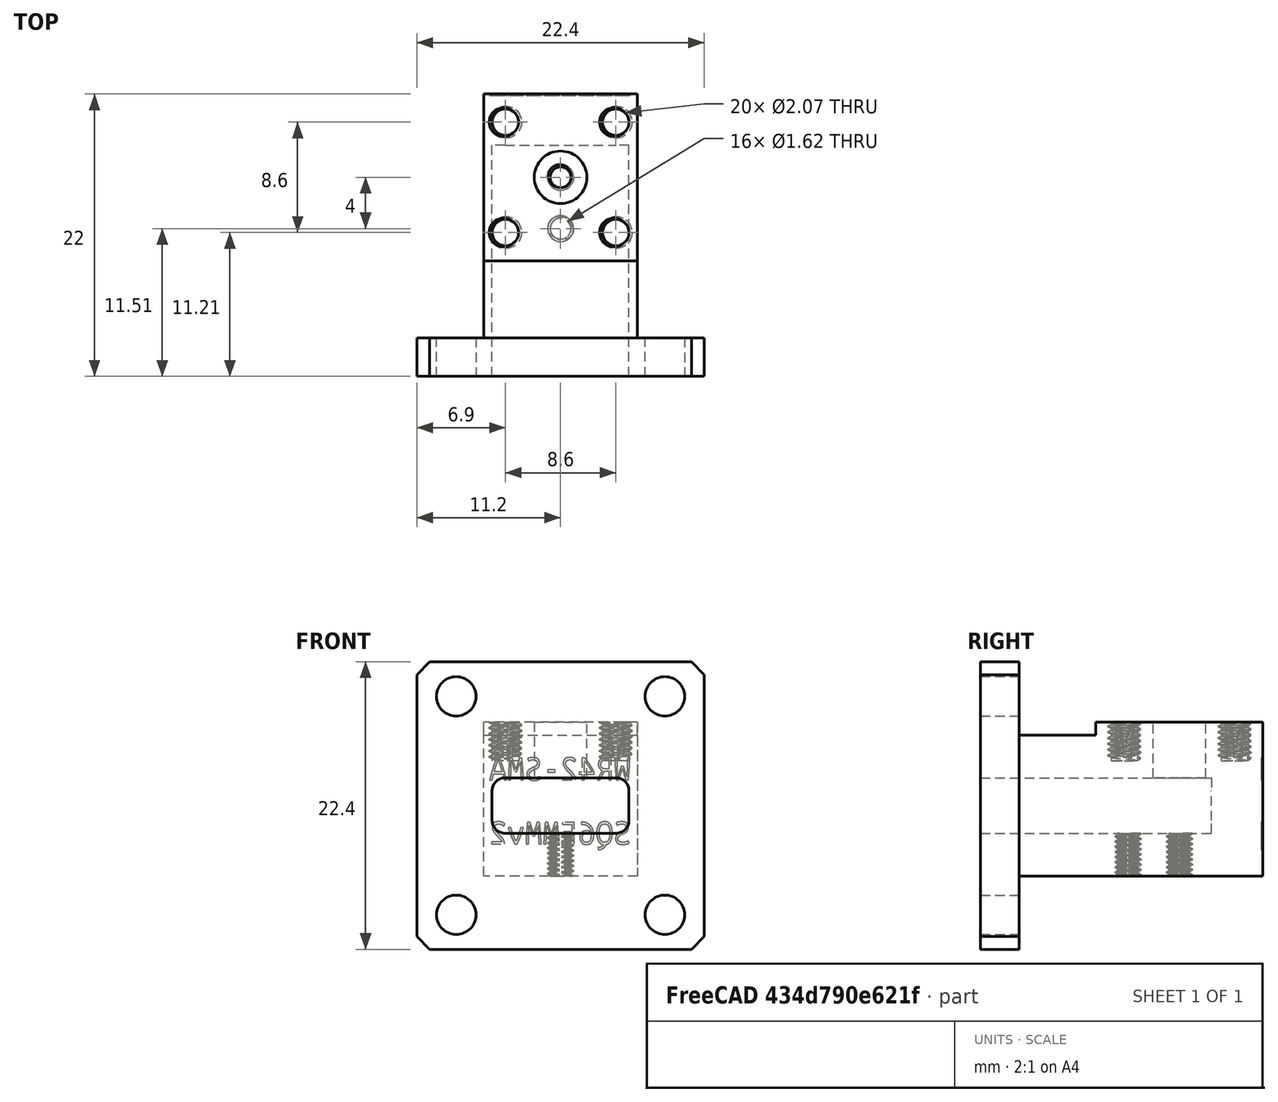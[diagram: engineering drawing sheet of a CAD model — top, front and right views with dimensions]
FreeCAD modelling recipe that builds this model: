
FCSTD DOCUMENT  (FreeCAD 1.0R38641 +468 (Git))
Label: WR42-SMA-narrow
License: All rights reserved
LicenseURL: https://en.wikipedia.org/wiki/All_rights_reserved
objects: Sketcher::SketchObject×7, PartDesign::Chamfer×4, PartDesign::Pocket×4, PartDesign::Pad×3, TechDraw::DrawViewPart×3, TechDraw::DrawViewBalloon×3, PartDesign::Hole×2, Part::Part2DObjectPython×2, TechDraw::DrawSVGTemplate×1, PartDesign::Body×1, TechDraw::DrawPage×1
note: 56 computed .brp shape members not serialized (recipe doc carries the construction recipe); baked Part::Feature solids carry a one-line shape summary decoded from their .brp

FEATURE [Sketcher::SketchObject] Sketch
  ArcFitTolerance = 0
  AttachmentSupport = -> [XZ_Plane]
  FullyConstrained = true
  MakeInternals = false
  MapMode = 5
  Placement = pos=(0,0,0) rot=(1,0,0;1.5708rad)
  sketch-geometry (9):
    g0: LineSegment StartX=-11.2 StartY=11.2 StartZ=0 EndX=-11.2 EndY=-11.2 EndZ=0
    g1: LineSegment StartX=-11.2 StartY=-11.2 StartZ=0 EndX=11.2 EndY=-11.2 EndZ=0
    g2: LineSegment StartX=11.2 StartY=-11.2 StartZ=0 EndX=11.2 EndY=11.2 EndZ=0
    g3: LineSegment StartX=11.2 StartY=11.2 StartZ=0 EndX=-11.2 EndY=11.2 EndZ=0
    g4: GeomPoint [constr] X=0 Y=0 Z=0
    g5: Circle CenterX=-8.13 CenterY=8.51 CenterZ=0 NormalX=0 NormalY=0 NormalZ=1 AngleXU=0 Radius=1.535
    g6: Circle CenterX=8.13 CenterY=8.51 CenterZ=0 NormalX=0 NormalY=0 NormalZ=1 AngleXU=0 Radius=1.535
    g7: Circle CenterX=8.13 CenterY=-8.51 CenterZ=0 NormalX=0 NormalY=0 NormalZ=1 AngleXU=0 Radius=1.535
    g8: Circle CenterX=-8.13 CenterY=-8.51 CenterZ=0 NormalX=0 NormalY=0 NormalZ=1 AngleXU=0 Radius=1.535
  constraints (24):
    c: Coincident(g0,g1)
    c: Coincident(g1,g2)
    c: Coincident(g2,g3)
    c: Coincident(g3,g0)
    c: Horizontal(g1)
    c: Horizontal(g3)
    c: Vertical(g0)
    c: Vertical(g2)
    c: Symmetric(g1,g0,g4)
    c: Coincident(g4,g-1)
    c: DistanceY(g2,g2) = 22.4
    c: DistanceX(g3,g3) = 22.4
    c: Diameter(g5) = 3.07
    c: Equal(g5,g6)
    c: Equal(g5,g8)
    c: Equal(g5,g7)
    c: DistanceX(g4,g6) = 8.13
    c: DistanceX(g5,g4) = 8.13
    c: DistanceX(g8,g4) = 8.13
    c: DistanceX(g4,g7) = 8.13
    c: DistanceY(g4,g5) = 8.51
    c: DistanceY(g4,g6) = 8.51
    c: DistanceY(g7,g4) = 8.51
    c: DistanceY(g8,g4) = 8.51
FEATURE [PartDesign::Pad] Pad
  Direction = (0,-1,2e-16)
  Length = 3
  Length2 = 10
  Placement = pos=(0,0,0) rot=(1,0,0;1.5708rad)
  Profile = -> Sketch
  ReferenceAxis = -> Sketch [N_Axis]
  Suppressed = false
  Type = 0
FEATURE [PartDesign::Chamfer] Chamfer
  Angle = 45
  Base = -> Pad [Edge8]
  BaseFeature = -> Pad
  ChamferType = 0
  FlipDirection = false
  Placement = pos=(0,0,0) rot=(1,0,0;1.5708rad)
  Size = 1
  Size2 = 1
  SupportTransform = false
  Suppressed = false
  UseAllEdges = false
FEATURE [PartDesign::Chamfer] Chamfer001
  Angle = 45
  Base = -> Chamfer [Edge23]
  BaseFeature = -> Chamfer
  ChamferType = 0
  FlipDirection = false
  Placement = pos=(0,0,0) rot=(1,0,0;1.5708rad)
  Size = 1
  Size2 = 1
  SupportTransform = false
  Suppressed = false
  UseAllEdges = false
FEATURE [PartDesign::Chamfer] Chamfer002
  Angle = 45
  Base = -> Chamfer001 [Edge20]
  BaseFeature = -> Chamfer001
  ChamferType = 0
  FlipDirection = false
  Placement = pos=(0,0,0) rot=(1,0,0;1.5708rad)
  Size = 1
  Size2 = 1
  SupportTransform = false
  Suppressed = false
  UseAllEdges = false
FEATURE [PartDesign::Chamfer] Chamfer003
  Angle = 45
  Base = -> Chamfer002 [Edge19]
  BaseFeature = -> Chamfer002
  ChamferType = 0
  FlipDirection = false
  Placement = pos=(0,0,0) rot=(1,0,0;1.5708rad)
  Size = 1
  Size2 = 1
  SupportTransform = false
  Suppressed = false
  UseAllEdges = false
FEATURE [Sketcher::SketchObject] Sketch001
  ArcFitTolerance = 0
  AttachmentSupport = -> [Chamfer003]
  ExternalGeometry = -> [Chamfer003]
  FullyConstrained = true
  MakeInternals = false
  MapMode = 5
  Placement = pos=(0,0,0) rot=(-1,0,0;1.5708rad)
  sketch-geometry (5):
    g0: LineSegment StartX=-6 StartY=5.5 StartZ=0 EndX=-6 EndY=-5.5 EndZ=0
    g1: LineSegment StartX=-6 StartY=-5.5 StartZ=0 EndX=6 EndY=-5.5 EndZ=0
    g2: LineSegment StartX=6 StartY=-5.5 StartZ=0 EndX=6 EndY=5.5 EndZ=0
    g3: LineSegment StartX=6 StartY=5.5 StartZ=0 EndX=-6 EndY=5.5 EndZ=0
    g4: GeomPoint [constr] X=0 Y=0 Z=0
  constraints (12):
    c: Coincident(g0,g1)
    c: Coincident(g1,g2)
    c: Coincident(g2,g3)
    c: Coincident(g3,g0)
    c: Horizontal(g1)
    c: Horizontal(g3)
    c: Vertical(g0)
    c: Vertical(g2)
    c: Symmetric(g1,g0,g4)
    c: Coincident(g4,g-1)
    c: DistanceY(g2,g2) = 11
    c: DistanceX(g3,g3) = 12
FEATURE [PartDesign::Pad] Pad001
  BaseFeature = -> Chamfer003
  Direction = (0,1,2e-16)
  Length = 19
  Length2 = 10
  Placement = pos=(0,0,0) rot=(1,0,0;1.5708rad)
  Profile = -> Sketch001
  ReferenceAxis = -> Sketch001 [N_Axis]
  Suppressed = false
  Type = 0
FEATURE [Sketcher::SketchObject] Sketch002
  ArcFitTolerance = 0
  AttachmentSupport = -> [Pad001]
  FullyConstrained = true
  MakeInternals = false
  MapMode = 5
  Placement = pos=(0,-3,0) rot=(1,0,0;1.5708rad)
  sketch-geometry (13):
    g0: LineSegment StartX=-5.334 StartY=-1.159 StartZ=0 EndX=-5.334 EndY=1.159 EndZ=0
    g1: LineSegment StartX=-4.334 StartY=2.159 StartZ=0 EndX=4.334 EndY=2.159 EndZ=0
    g2: LineSegment StartX=5.334 StartY=1.159 StartZ=0 EndX=5.334 EndY=-1.159 EndZ=0
    g3: LineSegment StartX=4.334 StartY=-2.159 StartZ=0 EndX=-4.334 EndY=-2.159 EndZ=0
    g4: GeomPoint [constr] X=0 Y=0 Z=0
    g5: ArcOfCircle CenterX=-4.334 CenterY=1.159 CenterZ=0 NormalX=0 NormalY=0 NormalZ=1 AngleXU=0 Radius=1 StartAngle=1.5708 EndAngle=3.14159
    g6: GeomPoint [constr] X=-5.334 Y=2.159 Z=0
    g7: ArcOfCircle CenterX=4.334 CenterY=1.159 CenterZ=0 NormalX=0 NormalY=0 NormalZ=1 AngleXU=0 Radius=1 StartAngle=0 EndAngle=1.5708
    g8: GeomPoint [constr] X=5.334 Y=2.159 Z=0
    g9: ArcOfCircle CenterX=4.334 CenterY=-1.159 CenterZ=0 NormalX=0 NormalY=0 NormalZ=1 AngleXU=0 Radius=1 StartAngle=4.71239 EndAngle=6.28319
    g10: GeomPoint [constr] X=5.334 Y=-2.159 Z=0
    g11: ArcOfCircle CenterX=-4.334 CenterY=-1.159 CenterZ=0 NormalX=0 NormalY=0 NormalZ=1 AngleXU=0 Radius=1 StartAngle=3.14159 EndAngle=4.71239
    g12: GeomPoint [constr] X=-5.334 Y=-2.159 Z=0
  constraints (28):
    c: Horizontal(g1)
    c: Horizontal(g3)
    c: Vertical(g0)
    c: Vertical(g2)
    c: Symmetric(g8,g12,g4)
    c: Coincident(g4,g-1)
    c: PointOnObject(g6,g1)
    c: PointOnObject(g6,g0)
    c: Tangent(g1,g5) = 1.5708
    c: Tangent(g0,g5) = 1.5708
    c: PointOnObject(g8,g1)
    c: PointOnObject(g8,g2)
    c: Tangent(g1,g7) = 1.5708
    c: Tangent(g2,g7) = 1.5708
    c: PointOnObject(g10,g2)
    c: PointOnObject(g10,g3)
    c: Tangent(g2,g9) = 1.5708
    c: Tangent(g3,g9) = 1.5708
    c: PointOnObject(g12,g3)
    c: PointOnObject(g12,g0)
    c: Tangent(g3,g11) = 1.5708
    c: Tangent(g0,g11) = 1.5708
    c: Radius(g5) = 1
    c: Radius(g7) = 1
    c: Radius(g9) = 1
    c: Radius(g11) = 1
    c: DistanceX(g0,g2) = 10.668
    c: DistanceY(g3,g1) = 4.318
FEATURE [PartDesign::Pocket] Pocket
  BaseFeature = -> Pad001
  Direction = (0,1,-2e-16)
  Length = 18
  Length2 = 5
  Placement = pos=(0,0,0) rot=(1,0,0;1.5708rad)
  Profile = -> Sketch002
  ReferenceAxis = -> Sketch002 [N_Axis]
  Suppressed = false
  Type = 0
FEATURE [Sketcher::SketchObject] Sketch005
  ArcFitTolerance = 0
  AttachmentSupport = -> [Pocket]
  ExternalGeometry = -> [Pocket]
  FullyConstrained = true
  MakeInternals = false
  MapMode = 45
  Placement = pos=(2e-16,9.5,5.5) rot=(0,0,1;0rad)
  sketch-geometry (4):
    g0: LineSegment StartX=6 StartY=-3.5 StartZ=0 EndX=-6 EndY=-3.5 EndZ=0
    g1: LineSegment StartX=-6 StartY=-3.5 StartZ=0 EndX=-6 EndY=9.5 EndZ=0
    g2: LineSegment StartX=-6 StartY=9.5 StartZ=0 EndX=6 EndY=9.5 EndZ=0
    g3: LineSegment StartX=6 StartY=9.5 StartZ=0 EndX=6 EndY=-3.5 EndZ=0
  constraints (12):
    c: Coincident(g0,g1)
    c: Coincident(g1,g2)
    c: Coincident(g2,g3)
    c: Coincident(g3,g0)
    c: Horizontal(g0)
    c: Horizontal(g2)
    c: Vertical(g1)
    c: Vertical(g3)
    c: DistanceX(g2,g2) = 12
    c: DistanceX(g1,g-1) = 6
    c: DistanceY(g1,g-3) = 0
    c: DistanceY(g3,g3) = 13
FEATURE [PartDesign::Pad] Pad002
  BaseFeature = -> Pocket
  Direction = (0,0,1)
  Length = 1
  Length2 = 10
  Placement = pos=(0,0,0) rot=(1,0,0;1.5708rad)
  Profile = -> Sketch005
  ReferenceAxis = -> Sketch005 [N_Axis]
  Refine = true
  Suppressed = false
  Type = 0
FEATURE [Sketcher::SketchObject] Sketch006
  ArcFitTolerance = 0
  AttachmentSupport = -> [Pad002]
  ExternalGeometry = -> [Pad002]
  FullyConstrained = true
  MakeInternals = false
  MapMode = 5
  Placement = pos=(0,0,6.5) rot=(0,0,1;3.14159rad)
  sketch-geometry (1):
    g0: Circle CenterX=0 CenterY=-12.51 CenterZ=0 NormalX=0 NormalY=0 NormalZ=1 AngleXU=0 Radius=2.05
  constraints (3):
    c: PointOnObject(g0,g-2)
    c: Diameter(g0) = 4.1
    c: DistanceY(g-3,g0) = 2.49
FEATURE [PartDesign::Pocket] Pocket001
  BaseFeature = -> Pad002
  Direction = (0,0,-1)
  Length = 5
  Length2 = 5
  Placement = pos=(0,0,0) rot=(1,0,0;1.5708rad)
  Profile = -> Sketch006
  ReferenceAxis = -> Sketch006 [N_Axis]
  Suppressed = false
  Type = 2
FEATURE [Sketcher::SketchObject] Sketch007
  ArcFitTolerance = 0
  AttachmentSupport = -> [Pocket001]
  ExternalGeometry = -> [Pocket001]
  FullyConstrained = true
  MakeInternals = false
  MapMode = 5
  Placement = pos=(0,0,6.5) rot=(0,0,1;3.14159rad)
  sketch-geometry (4):
    g0: Circle CenterX=-4.3 CenterY=-8.21 CenterZ=0 NormalX=0 NormalY=0 NormalZ=1 AngleXU=0 Radius=1.025
    g1: Circle CenterX=4.3 CenterY=-8.21 CenterZ=0 NormalX=0 NormalY=0 NormalZ=1 AngleXU=0 Radius=1.025
    g2: Circle CenterX=4.3 CenterY=-16.81 CenterZ=0 NormalX=0 NormalY=0 NormalZ=1 AngleXU=0 Radius=1.025
    g3: Circle CenterX=-4.3 CenterY=-16.81 CenterZ=0 NormalX=0 NormalY=0 NormalZ=1 AngleXU=0 Radius=1.025
  constraints (12):
    c: Diameter(g0) = 2.05
    c: Equal(g1,g0)
    c: Equal(g0,g2)
    c: Equal(g0,g3)
    c: DistanceX(g0,g-3) = 4.3
    c: DistanceY(g-3,g0) = 4.3
    c: DistanceX(g-3,g1) = 4.3
    c: DistanceX(g-3,g2) = 4.3
    c: DistanceX(g3,g-3) = 4.3
    c: DistanceY(g-3,g1) = 4.3
    c: DistanceY(g2,g-3) = 4.3
    c: DistanceY(g3,g-3) = 4.3
FEATURE [PartDesign::Hole] Hole
  BaseFeature = -> Pocket001
  CustomThreadClearance = 0
  Depth = 3
  DepthType = 0
  Diameter = 2.07
  DrillForDepth = false
  DrillPoint = 0
  DrillPointAngle = 118
  HoleCutCountersinkAngle = 90
  HoleCutCustomValues = false
  HoleCutDepth = 0
  HoleCutDiameter = 6.1
  HoleCutType = 0
  ModelThread = true
  Placement = pos=(0,0,0) rot=(1,0,0;1.5708rad)
  Profile = -> Sketch007
  Suppressed = false
  Tapered = false
  TaperedAngle = 90
  ThreadClass = 0
  ThreadDepth = 3
  ThreadDepthType = 0
  ThreadDirection = 0
  ThreadFit = 0
  ThreadSize = 8
  ThreadType = 1
  Threaded = true
  UseCustomThreadClearance = false
FEATURE [Part::Part2DObjectPython] ShapeString  # Draft 2D object (typed FeaturePython)
  FontFile = <path>
  Fuse = false
  Justification = 6
  JustificationReference = 0
  KeepLeftMargin = true
  MakeFace = true
  ObliqueAngle = 0
  Placement = pos=(5.5,19,2) rot=(0,0.707107,0.707107;3.14159rad)
  ScaleToSize = false
  Size = 0.9
  String = WR42-SMA
  Tracking = 0
FEATURE [PartDesign::Pocket] Pocket002
  BaseFeature = -> Hole
  Direction = (-1e-16,-1,2e-16)
  Length = 0.1
  Length2 = 5
  Placement = pos=(0,0,0) rot=(1,0,0;1.5708rad)
  Profile = -> ShapeString
  ReferenceAxis = -> ShapeString [N_Axis]
  Suppressed = false
  Type = 0
FEATURE [Part::Part2DObjectPython] ShapeString001  # Draft 2D object (typed FeaturePython)
  FontFile = <path>
  Fuse = false
  Justification = 6
  JustificationReference = 0
  KeepLeftMargin = true
  MakeFace = true
  ObliqueAngle = 0
  Placement = pos=(5.5,19,-3) rot=(0,0.707107,0.707107;3.14159rad)
  ScaleToSize = false
  Size = 0.9
  String = SQ6EMMv2
  Tracking = 0
FEATURE [PartDesign::Pocket] Pocket003
  BaseFeature = -> Pocket002
  Direction = (-1e-16,-1,2e-16)
  Length = 0.1
  Length2 = 5
  Placement = pos=(0,0,0) rot=(1,0,0;1.5708rad)
  Profile = -> ShapeString001
  ReferenceAxis = -> ShapeString001 [N_Axis]
  Suppressed = false
  Type = 0
FEATURE [TechDraw::DrawSVGTemplate] Template
  EditableTexts = Drawing_number=01; FC-Date=31/3/2025; FC-SC=2 : 1; FC-SH=01; FC-Title=WR42-SMA-narrow; Subtitle=Threads and precision perspective; Weight=n/a
  Height = 210
  Orientation = 1
  Template = <path>
  Width = 297
FEATURE [TechDraw::DrawViewPart] View  label="Front"
  CoarseView = false
  Direction = (0,-1,0)
  Focus = 100
  HardHidden = false
  IsoCount = 0
  IsoHidden = false
  IsoVisible = false
  LockPosition = false
  Perspective = false
  Rotation = 0
  Scale = 2
  ScaleType = 2
  ScrubCount = 0
  SeamHidden = false
  SeamVisible = false
  SmoothHidden = false
  SmoothVisible = true
  Source = -> [Pocket003]
  X = 73.0258
  XDirection = (1,0,0)
  Y = 63.0699
FEATURE [TechDraw::DrawViewBalloon] Balloon
  BubbleShape = 6
  EndType = 0
  EndTypeScale = 1
  KinkLength = 5
  LockPosition = false
  OriginX = 0.700083
  OriginY = 0.0873544
  Rotation = 0
  ScaleType = 0
  ShapeScale = 1
  SourceView = -> View
  Text = internal dimensions high precision
  TextWrapLen = -1
  X = 43.3706
  Y = 2.40017
FEATURE [Sketcher::SketchObject] Sketch008
  ArcFitTolerance = 1e-06
  AttachmentSupport = -> [Pocket003]
  ExternalGeometry = -> [Pocket003]
  FullyConstrained = true
  MakeInternals = false
  MapMode = 5
  Placement = pos=(0,0,-5.5) rot=(1,0,0;3.14159rad)
  sketch-geometry (2):
    g0: Circle CenterX=0 CenterY=-12.51 CenterZ=0 NormalX=0 NormalY=0 NormalZ=1 AngleXU=0 Radius=0.75
    g1: Circle CenterX=0 CenterY=-8.51 CenterZ=0 NormalX=0 NormalY=0 NormalZ=1 AngleXU=0 Radius=0.75
  constraints (5):
    c: Diameter(g0) = 1.5
    c: Coincident(g0,g-3)
    c: PointOnObject(g1,g-2)
    c: Equal(g0,g1)
    c: DistanceY(g0,g1) = 4
FEATURE [PartDesign::Hole] Hole001
  BaseFeature = -> Pocket003
  CustomThreadClearance = 0
  Depth = 4
  DepthType = 0
  Diameter = 1.619
  DrillForDepth = false
  DrillPoint = 1
  DrillPointAngle = 118
  HoleCutCountersinkAngle = 90
  HoleCutCustomValues = false
  HoleCutDepth = 0
  HoleCutDiameter = 6.1
  HoleCutType = 0
  ModelThread = true
  Placement = pos=(0,0,0) rot=(1,0,0;1.5708rad)
  Profile = -> Sketch008
  Refine = true
  Suppressed = false
  Tapered = false
  TaperedAngle = 90
  ThreadClass = 0
  ThreadDepth = 4
  ThreadDepthType = 0
  ThreadDirection = 0
  ThreadFit = 0
  ThreadSize = 6
  ThreadType = 1
  Threaded = true
  UseCustomThreadClearance = false
FEATURE [PartDesign::Body] Body
  AllowCompound = false
  Group = -> [Sketch,Pad,Chamfer,Chamfer001,Chamfer002,Chamfer003,Sketch001,Pad001,Sketch002,Pocket,Sketch005,Pad002,Sketch006,Pocket001,Sketch007,Hole,ShapeString,Pocket002,ShapeString001,Pocket003,Sketch008,Hole001]
  Origin = -> Origin
  Tip = -> Hole001
FEATURE [TechDraw::DrawViewPart] View001  label="Top"
  CoarseView = false
  Direction = (0,0,1)
  Focus = 100
  HardHidden = false
  IsoCount = 0
  IsoHidden = false
  IsoVisible = false
  LockPosition = false
  Perspective = false
  Rotation = 0
  Scale = 2
  ScaleType = 2
  ScrubCount = 0
  SeamHidden = false
  SeamVisible = false
  SmoothHidden = false
  SmoothVisible = true
  Source = -> [Hole001]
  X = 74.4235
  XDirection = (1,0,0)
  Y = 144.484
FEATURE [TechDraw::DrawViewPart] View002  label="Bottom"
  CoarseView = false
  Direction = (0,0,-1)
  Focus = 100
  HardHidden = false
  IsoCount = 0
  IsoHidden = false
  IsoVisible = false
  LockPosition = false
  Perspective = false
  Rotation = 0
  Scale = 2
  ScaleType = 2
  ScrubCount = 0
  SeamHidden = false
  SeamVisible = false
  SmoothHidden = false
  SmoothVisible = true
  Source = -> [Hole001]
  X = 225.372
  XDirection = (1,0,0)
  Y = 152.521
FEATURE [TechDraw::DrawViewBalloon] Balloon001
  BubbleShape = 6
  EndType = 0
  EndTypeScale = 1
  KinkLength = 5
  LockPosition = false
  OriginX = 0.525374
  OriginY = -4.28037
  Rotation = 0
  ScaleType = 0
  ShapeScale = 1
  SourceView = -> View002
  Text = 2 x M2 0,4
  TextWrapLen = -1
  X = 15.9413
  Y = -25.3785
FEATURE [TechDraw::DrawViewBalloon] Balloon002
  BubbleShape = 6
  EndType = 0
  EndTypeScale = 1
  KinkLength = 5
  LockPosition = false
  OriginX = -4.01705
  OriginY = 9.34692
  Rotation = 0
  ScaleType = 0
  ShapeScale = 1
  SourceView = -> View001
  Text = 4 x M2.5 0,45
  TextWrapLen = -1
  X = 21.0079
  Y = 19.1722
FEATURE [TechDraw::DrawPage] Page  label="2D drawing"
  KeepUpdated = true
  NextBalloonIndex = 4
  ProjectionType = 0
  Template = -> Template
  Views = -> [View,View001,View002,Balloon,Balloon001,Balloon002]
note: 3 file-system paths scrubbed to <path> (originals preserved in the JSON sidecar)
